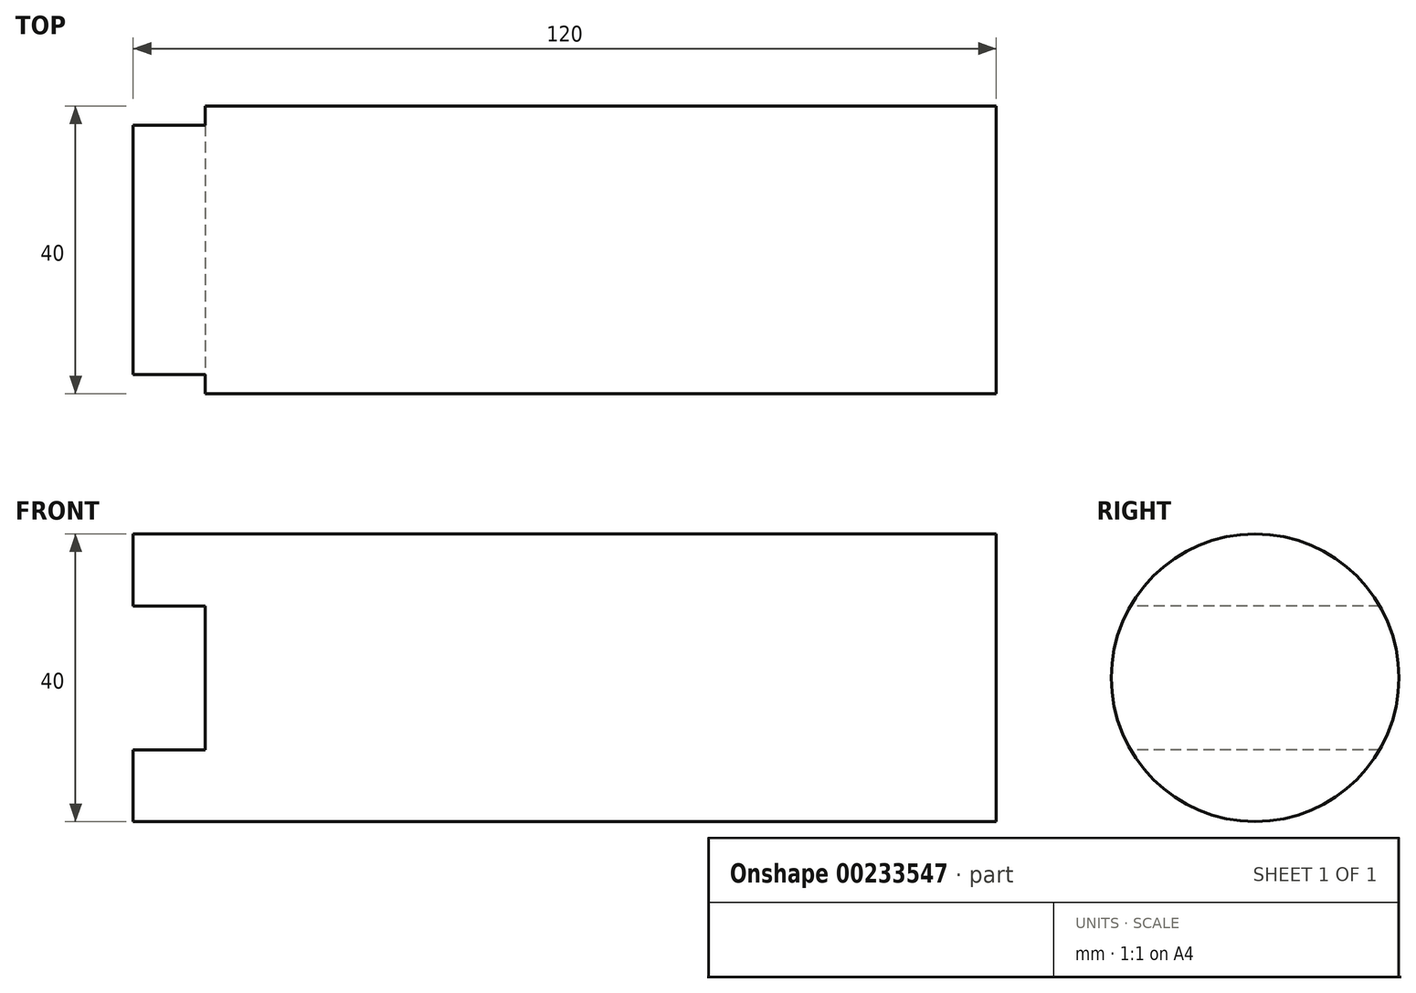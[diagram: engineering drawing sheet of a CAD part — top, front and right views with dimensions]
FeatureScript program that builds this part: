
annotation { "Feature Type Name" : "Feature", "Feature Type Description" : "" }
export const myFeature = defineFeature(function(context is Context, id is Id, definition is map)
    precondition{}
    {
        {
            var Q0;
            Q0=qCreatedBy(makeId("Front.planeOp"),FACE);
            var sketch = newSketch(context, id + "F0", { "sketchPlane" : qUnion([Q0])});
            skLineSegment(sketch, "E0", {"start": v(0, 0) * mm, "end": v(0, 10) * mm});
            skLineSegment(sketch, "E1", {"start": v(0, 10) * mm, "end": v(-10, 10) * mm});
            skLineSegment(sketch, "E2", {"start": v(-10, 10) * mm, "end": v(-10, 20) * mm});
            skLineSegment(sketch, "E3", {"start": v(-10, 20) * mm, "end": v(110, 20) * mm});
            skLineSegment(sketch, "E4", {"start": v(110, 20) * mm, "end": v(110, 0) * mm});
            skLineSegment(sketch, "E5", {"start": v(110, 0) * mm, "end": v(0, 0) * mm});
            skLineSegment(sketch, "E6", {"start": v(-10, 10) * mm, "end": v(-10, 0) * mm});
            skLineSegment(sketch, "E7", {"start": v(-10, 0) * mm, "end": v(0, 0) * mm});
            skLineSegment(sketch, "E8.MirrorCS", {"start": v(0, 0) * mm, "end": v(0, -10) * mm});
            skLineSegment(sketch, "E9.MirrorCS", {"start": v(-10, -10) * mm, "end": v(-10, 0) * mm});
            skLineSegment(sketch, "E10.MirrorCS", {"start": v(0, -10) * mm, "end": v(-10, -10) * mm});
            skSolve(sketch);
        }
        {
            var Q0;
            Q0=makeQuery(id+"F0.imprint","IMPRINT",FACE,{"disambiguationData":[TD([[makeQuery(id+"F0.imprint","IMPRINT",EDGE,{"derivedFrom":sQuery(id+"F0.wireOp",EDGE,"E0")}),1.0]])]});
            var Q1;
            Q1=makeQuery(id+"F0.imprint","IMPRINT",FACE,{"disambiguationData":[TD([[makeQuery(id+"F0.imprint","IMPRINT",EDGE,{"derivedFrom":sQuery(id+"F0.wireOp",EDGE,"E0")}),-1.0]])]});
            var Q2;
            Q2=sQuery(id+"F0.wireOp",EDGE,"E5");
            revolve(context, id + "F1", {"entities" : qUnion([Q0, Q1]), "axis" : qUnion([Q2]), "revolveType" : RevolveType.FULL});
        }
        {
            var Q0;
            Q0=makeQuery(id+"F0.imprint","IMPRINT",FACE,{"disambiguationData":[TD([[makeQuery(id+"F0.imprint","IMPRINT",EDGE,{"derivedFrom":sQuery(id+"F0.wireOp",EDGE,"E0")}),1.0]])]});
            var Q1;
            Q1=makeQuery(id+"F0.imprint","IMPRINT",FACE,{"disambiguationData":[TD([[makeQuery(id+"F0.imprint","IMPRINT",EDGE,{"derivedFrom":sQuery(id+"F0.wireOp",EDGE,"E7")}),-1.0]])]});
            extrude(context, id + "F2", {"entities" : qUnion([Q0, Q1]), "operationType" : NewBodyOperationType.REMOVE, "endBound" : BoundingType.SYMMETRIC, "oppositeDirection" : true, "depth" : 50 * mm});
        }
    });
